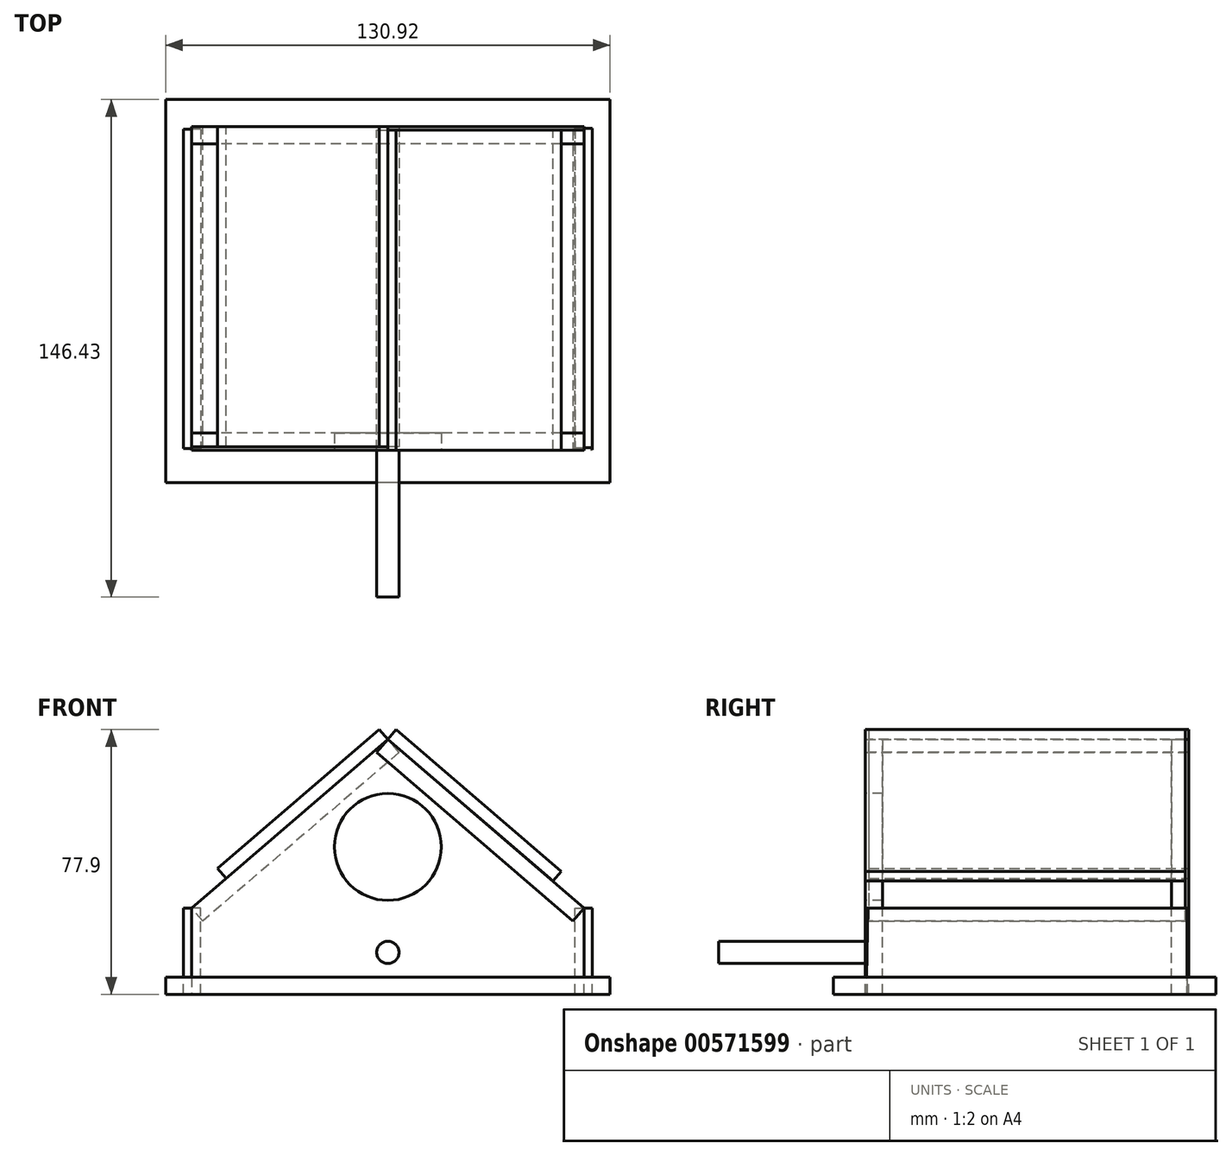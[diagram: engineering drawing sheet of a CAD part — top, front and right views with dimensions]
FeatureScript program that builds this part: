
annotation { "Feature Type Name" : "Feature", "Feature Type Description" : "" }
export const myFeature = defineFeature(function(context is Context, id is Id, definition is map)
    precondition{}
    {
        {
            var Q0;
            Q0=qCreatedBy(makeId("Top.planeOp"),FACE);
            var sketch = newSketch(context, id + "F0", { "sketchPlane" : qUnion([Q0])});
            skLineSegment(sketch, "E0", {"start": v(0, -56.23) * mm, "end": v(-65.46, -56.23) * mm});
            skLineSegment(sketch, "E1", {"start": v(-65.46, -56.23) * mm, "end": v(-65.46, 56.51) * mm});
            skLineSegment(sketch, "E2", {"start": v(-65.46, 56.51) * mm, "end": v(0, 56.51) * mm});
            skLineSegment(sketch, "E3.MirrorCS", {"start": v(0, -56.23) * mm, "end": v(65.46, -56.23) * mm});
            skLineSegment(sketch, "E4.MirrorCS", {"start": v(65.46, -56.23) * mm, "end": v(65.46, 56.51) * mm});
            skLineSegment(sketch, "E5.MirrorCS", {"start": v(65.46, 56.51) * mm, "end": v(0, 56.51) * mm});
            skSolve(sketch);
        }
        {
            var Q0;
            Q0 = qSketchRegion(id + "F0", true);
            extrude(context, id + "F1", {"entities" : qUnion([Q0]), "depth" : 5.08 * mm, "offsetDistance" : 25.4 * mm});
        }
        {
            var Q0;
            Q0=qCreatedBy(makeId("Front.planeOp"),FACE);
            cPlane(context, id + "F2", {"entities" : qUnion([Q0]), "cplaneType" : CPlaneType.OFFSET, "offset" : 41.66 * mm, "width" : 152.4 * mm, "height" : 152.4 * mm});
        }
        {
            var Q0;
            Q0=qCreatedBy(id+"F2.planeOp",FACE);
            var sketch = newSketch(context, id + "F3", { "sketchPlane" : qUnion([Q0])});
            skLineSegment(sketch, "E6", {"start": v(57.84, 0) * mm, "end": v(57.84, 25.4) * mm});
            skLineSegment(sketch, "E7", {"start": v(57.84, 25.4) * mm, "end": v(0, 75) * mm});
            skLineSegment(sketch, "E8", {"start": v(0, 75) * mm, "end": v(-57.84, 25.4) * mm});
            skLineSegment(sketch, "E9", {"start": v(-57.84, 25.4) * mm, "end": v(-57.84, 0) * mm});
            skLineSegment(sketch, "E10", {"start": v(57.84, 0) * mm, "end": v(-57.84, 0) * mm});
            skSolve(sketch);
        }
        {
            var Q0;
            Q0 = qSketchRegion(id + "F3", true);
            extrude(context, id + "F4", {"entities" : qUnion([Q0]), "depth" : 5.08 * mm, "offsetDistance" : 25.4 * mm});
        }
        {
            var Q0;
            Q0=qCreatedBy(makeId("Right.planeOp"),FACE);
            cPlane(context, id + "F5", {"entities" : qUnion([Q0]), "cplaneType" : CPlaneType.OFFSET, "offset" : 60.2 * mm, "oppositeDirection" : true, "width" : 152.4 * mm, "height" : 152.4 * mm});
        }
        {
            var Q0;
            Q0=qCreatedBy(id+"F5.planeOp",FACE);
            var sketch = newSketch(context, id + "F6", { "sketchPlane" : qUnion([Q0])});
            skLineSegment(sketch, "E11", {"start": v(-46.17, 0) * mm, "end": v(-46.17, 25.4) * mm});
            skLineSegment(sketch, "E12", {"start": v(-46.17, 25.4) * mm, "end": v(47.8, 25.4) * mm});
            skLineSegment(sketch, "E13", {"start": v(47.8, 25.4) * mm, "end": v(47.8, 0) * mm});
            skLineSegment(sketch, "E14", {"start": v(47.8, 0) * mm, "end": v(-46.17, 0) * mm});
            skSolve(sketch);
        }
        {
            var Q0;
            Q0 = qSketchRegion(id + "F6", true);
            extrude(context, id + "F7", {"entities" : qUnion([Q0]), "depth" : 5.08 * mm, "offsetDistance" : 25.4 * mm});
        }
        {
            var Q0;
            Q0=qCreatedBy(makeId("Right.planeOp"),FACE);
            cPlane(context, id + "F8", {"entities" : qUnion([Q0]), "cplaneType" : CPlaneType.OFFSET, "offset" : 60.2 * mm, "width" : 152.4 * mm, "height" : 152.4 * mm});
        }
        {
            var Q0;
            Q0=qCreatedBy(id+"F8.planeOp",FACE);
            var sketch = newSketch(context, id + "F9", { "sketchPlane" : qUnion([Q0])});
            skLineSegment(sketch, "E15", {"start": v(-46.02, 25.4) * mm, "end": v(47.96, 25.4) * mm});
            skLineSegment(sketch, "E16", {"start": v(47.96, 25.4) * mm, "end": v(47.96, 0) * mm});
            skLineSegment(sketch, "E17", {"start": v(47.96, 0) * mm, "end": v(-46.57, 0) * mm});
            skLineSegment(sketch, "E18", {"start": v(-46.57, 0) * mm, "end": v(-46.02, 25.4) * mm});
            skSolve(sketch);
        }
        {
            var Q0;
            Q0 = qSketchRegion(id + "F9", true);
            extrude(context, id + "F10", {"entities" : qUnion([Q0]), "oppositeDirection" : true, "depth" : 5.08 * mm, "offsetDistance" : 25.4 * mm});
        }
        {
            var Q0;
            Q0=qCreatedBy(id+"F2.planeOp",FACE);
            cPlane(context, id + "F11", {"entities" : qUnion([Q0]), "cplaneType" : CPlaneType.OFFSET, "offset" : 90.17 * mm, "oppositeDirection" : true, "width" : 152.4 * mm, "height" : 152.4 * mm});
        }
        {
            var Q0;
            Q0=qCreatedBy(id+"F11.planeOp",FACE);
            var sketch = newSketch(context, id + "F12", { "sketchPlane" : qUnion([Q0])});
            skLineSegment(sketch, "E19", {"start": v(57.84, 0) * mm, "end": v(57.84, 25.4) * mm});
            skLineSegment(sketch, "E20", {"start": v(57.84, 25.4) * mm, "end": v(0, 75) * mm});
            skLineSegment(sketch, "E21", {"start": v(0, 75) * mm, "end": v(-57.84, 25.4) * mm});
            skLineSegment(sketch, "E22", {"start": v(-57.84, 25.4) * mm, "end": v(-57.84, 0) * mm});
            skLineSegment(sketch, "E23", {"start": v(-57.84, 0) * mm, "end": v(57.84, 0) * mm});
            skSolve(sketch);
        }
        {
            var Q0;
            Q0 = qSketchRegion(id + "F12", true);
            extrude(context, id + "F13", {"entities" : qUnion([Q0]), "depth" : 5.08 * mm, "offsetDistance" : 25.4 * mm});
        }
        {
            var Q0;
            Q0=makeQuery(id+"F4.opExtrude","SWEPT_FACE",FACE,{"disambiguationData":[OSD([sQuery(id+"F3.wireOp",EDGE,"E7")])]});
            var sketch = newSketch(context, id + "F14", { "sketchPlane" : qUnion([Q0])});
            skLineSegment(sketch, "E24", {"start": v(-48.83, -46.74) * mm, "end": v(-48.83, 47.5) * mm});
            skLineSegment(sketch, "E25", {"start": v(-48.83, 47.5) * mm, "end": v(27.37, 47.5) * mm});
            skLineSegment(sketch, "E26", {"start": v(27.37, 47.5) * mm, "end": v(27.37, -46.74) * mm});
            skLineSegment(sketch, "E27", {"start": v(27.37, -46.74) * mm, "end": v(-48.83, -46.74) * mm});
            skSolve(sketch);
        }
        {
            var Q0;
            Q0 = qSketchRegion(id + "F14", true);
            extrude(context, id + "F15", {"entities" : qUnion([Q0]), "oppositeDirection" : true, "depth" : 5.08 * mm, "offsetDistance" : 25.4 * mm});
        }
        {
            var Q0;
            Q0=makeQuery(id+"F13.opExtrude","SWEPT_FACE",FACE,{"disambiguationData":[OSD([sQuery(id+"F12.wireOp",EDGE,"E21")])]});
            var sketch = newSketch(context, id + "F16", { "sketchPlane" : qUnion([Q0])});
            skLineSegment(sketch, "E28", {"start": v(48.83, 48.51) * mm, "end": v(48.83, -45.72) * mm});
            skLineSegment(sketch, "E29", {"start": v(48.83, -45.72) * mm, "end": v(-27.37, -45.72) * mm});
            skLineSegment(sketch, "E30", {"start": v(-27.37, -45.72) * mm, "end": v(-27.37, 48.51) * mm});
            skLineSegment(sketch, "E31", {"start": v(-27.37, 48.51) * mm, "end": v(48.83, 48.51) * mm});
            skLineSegment(sketch, "E32", {"start": v(48.83, 48.51) * mm, "end": v(-27.37, 48.51) * mm});
            skSolve(sketch);
        }
        {
            var Q0;
            Q0 = qSketchRegion(id + "F16", true);
            extrude(context, id + "F17", {"entities" : qUnion([Q0]), "oppositeDirection" : true, "depth" : 5.08 * mm, "offsetDistance" : 25.4 * mm});
        }
        {
            var Q0;
            Q0=makeQuery(id+"F4.opExtrude","CAP_FACE",FACE,{"disambiguationData":[OSD([sQuery(id+"F3.wireOp",EDGE,"E6"),sQuery(id+"F3.wireOp",EDGE,"E7"),sQuery(id+"F3.wireOp",EDGE,"E8"),sQuery(id+"F3.wireOp",EDGE,"E9"),sQuery(id+"F3.wireOp",EDGE,"E10")])],"isStart":false});
            var sketch = newSketch(context, id + "F18", { "sketchPlane" : qUnion([Q0])});
            skCircle(sketch, "E33", {"center": v(0, 43.36) * mm, "radius": 15.74 * mm});
            skSolve(sketch);
        }
        {
            var Q0;
            Q0 = qSketchRegion(id + "F18", true);
            extrude(context, id + "F19", {"entities" : qUnion([Q0]), "operationType" : NewBodyOperationType.REMOVE, "oppositeDirection" : true, "depth" : 59.94 * mm, "offsetDistance" : 25.4 * mm});
        }
        {
            var Q0;
            Q0=makeQuery(id+"F4.opExtrude","CAP_FACE",FACE,{"disambiguationData":[OSD([sQuery(id+"F3.wireOp",EDGE,"E6"),sQuery(id+"F3.wireOp",EDGE,"E7"),sQuery(id+"F3.wireOp",EDGE,"E8"),sQuery(id+"F3.wireOp",EDGE,"E9"),sQuery(id+"F3.wireOp",EDGE,"E10")])],"isStart":false});
            var sketch = newSketch(context, id + "F20", { "sketchPlane" : qUnion([Q0])});
            skCircle(sketch, "E34", {"center": v(0, 12.3) * mm, "radius": 3.27 * mm});
            skSolve(sketch);
        }
        {
            var Q0;
            Q0 = qSketchRegion(id + "F20", true);
            extrude(context, id + "F21", {"entities" : qUnion([Q0]), "operationType" : NewBodyOperationType.ADD, "depth" : 43.18 * mm, "offsetDistance" : 25.4 * mm});
        }
        {
            var Q0;
            Q0=makeQuery(id+"F15.opExtrude","CAP_FACE",FACE,{"disambiguationData":[OSD([sQuery(id+"F14.wireOp",EDGE,"E24"),sQuery(id+"F14.wireOp",EDGE,"E25"),sQuery(id+"F14.wireOp",EDGE,"E26"),sQuery(id+"F14.wireOp",EDGE,"E27")])],"isStart":true});
            var sketch = newSketch(context, id + "F22", { "sketchPlane" : qUnion([Q0])});
            skLineSegment(sketch, "E35", {"start": v(-48.83, 47.5) * mm, "end": v(-48.83, -46.74) * mm});
            skLineSegment(sketch, "E36", {"start": v(-48.83, -46.74) * mm, "end": v(15.24, -46.74) * mm});
            skLineSegment(sketch, "E37", {"start": v(15.24, -46.74) * mm, "end": v(15.24, 47.5) * mm});
            skLineSegment(sketch, "E38", {"start": v(15.24, 47.5) * mm, "end": v(-48.83, 47.5) * mm});
            skSolve(sketch);
        }
        {
            var Q0;
            Q0 = qSketchRegion(id + "F22", true);
            extrude(context, id + "F23", {"entities" : qUnion([Q0]), "depth" : 3.8 * mm, "offsetDistance" : 25.4 * mm});
        }
        {
            var Q0;
            Q0=makeQuery(id+"F17.opExtrude","CAP_FACE",FACE,{"disambiguationData":[OSD([sQuery(id+"F16.wireOp",EDGE,"E29"),sQuery(id+"F16.wireOp",EDGE,"E30"),sQuery(id+"F16.wireOp",EDGE,"E28"),sQuery(id+"F16.wireOp",EDGE,"E32")])],"isStart":true});
            var sketch = newSketch(context, id + "F24", { "sketchPlane" : qUnion([Q0])});
            skLineSegment(sketch, "E39", {"start": v(48.83, 48.51) * mm, "end": v(48.83, -45.72) * mm});
            skLineSegment(sketch, "E40", {"start": v(48.83, -45.72) * mm, "end": v(-13.92, -45.72) * mm});
            skLineSegment(sketch, "E41", {"start": v(-13.92, -45.72) * mm, "end": v(-13.92, 48.51) * mm});
            skLineSegment(sketch, "E42", {"start": v(-13.92, 48.51) * mm, "end": v(48.83, 48.51) * mm});
            skSolve(sketch);
        }
        {
            var Q0;
            Q0 = qSketchRegion(id + "F24", true);
            extrude(context, id + "F25", {"entities" : qUnion([Q0]), "depth" : 3.8 * mm, "offsetDistance" : 25.4 * mm});
        }
    });
